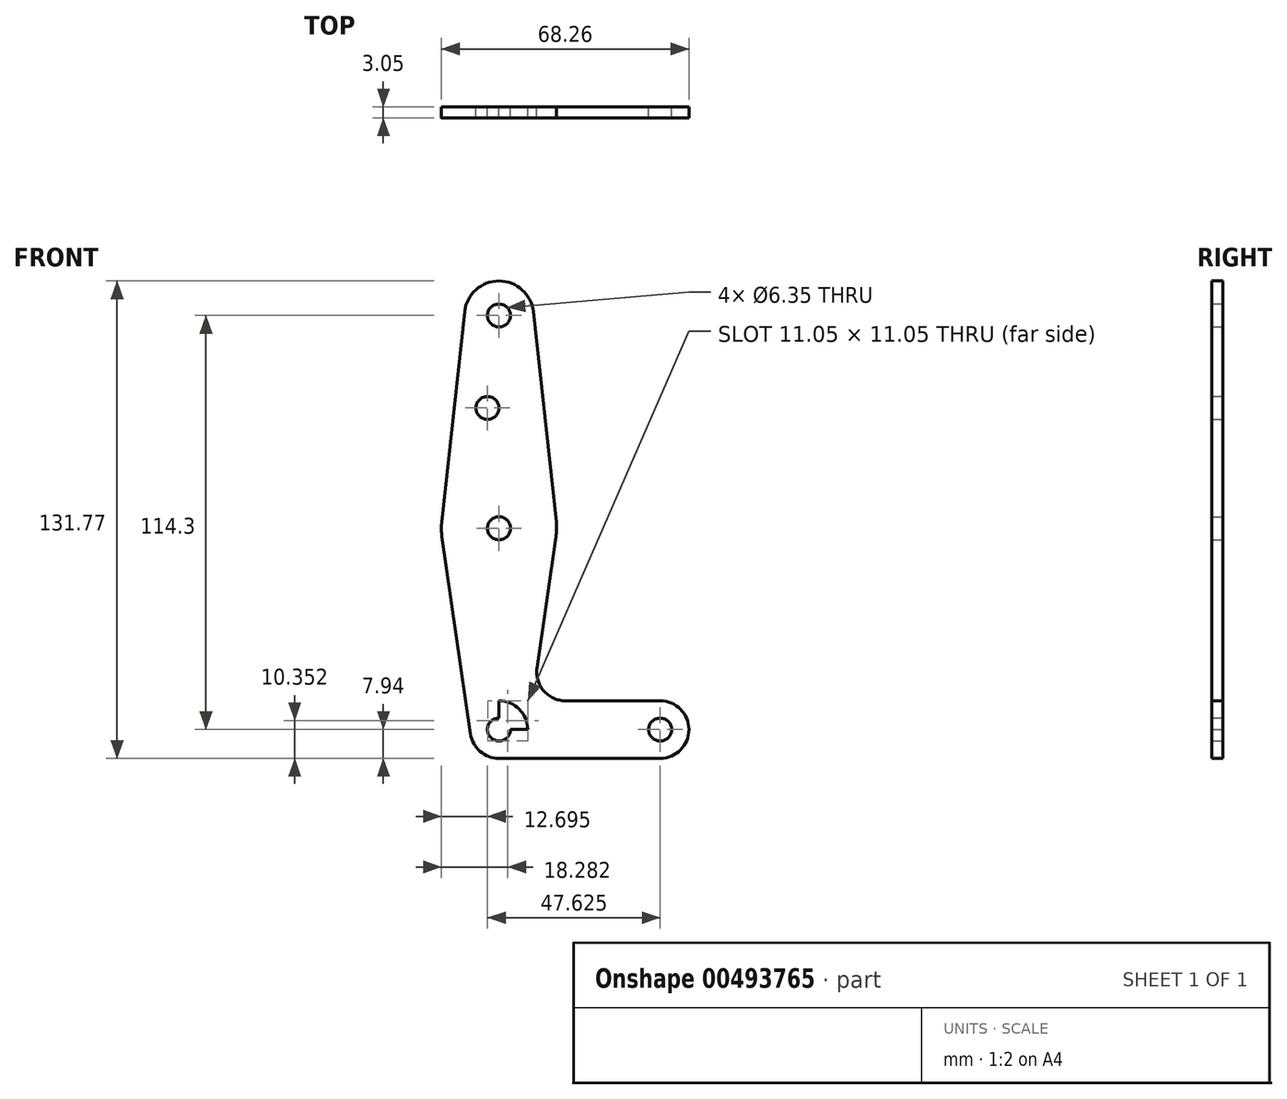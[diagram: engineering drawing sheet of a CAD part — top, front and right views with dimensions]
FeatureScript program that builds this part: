
annotation { "Feature Type Name" : "Feature", "Feature Type Description" : "" }
export const myFeature = defineFeature(function(context is Context, id is Id, definition is map)
    precondition{}
    {
        {
            var Q0;
            Q0=qCreatedBy(makeId("Front.planeOp"),FACE);
            var sketch = newSketch(context, id + "F0", { "sketchPlane" : qUnion([Q0])});
            skLineSegment(sketch, "E0", {"start": v(0, 0) * mm, "end": v(0, 114.3) * mm});
            skLineSegment(sketch, "E1", {"start": v(0, 0) * mm, "end": v(44.45, 0) * mm});
            skCircle(sketch, "E2", {"center": v(0, 0) * mm, "radius": 7.94 * mm});
            skCircle(sketch, "E3", {"center": v(0, 114.3) * mm, "radius": 9.53 * mm});
            skCircle(sketch, "E4", {"center": v(44.45, 0) * mm, "radius": 7.94 * mm});
            skCircle(sketch, "E5", {"center": v(0, 55.56) * mm, "radius": 15.87 * mm});
            skLineSegment(sketch, "E6", {"start": v(9.47, 115.33) * mm, "end": v(15.78, 57.28) * mm});
            skLineSegment(sketch, "E7", {"start": v(-9.47, 115.33) * mm, "end": v(-15.8, 57.15) * mm});
            skPoint(sketch, "E7.endSnap0", {"position": v(0, 57.15) * mm});
            skLineSegment(sketch, "E8", {"start": v(-15.71, 53.3) * mm, "end": v(-7.86, -1.13) * mm});
            skLineSegment(sketch, "E9", {"start": v(15.71, 53.3) * mm, "end": v(10.48, 17.02) * mm});
            skLineSegment(sketch, "E10", {"start": v(18.35, 7.94) * mm, "end": v(44.45, 7.94) * mm});
            skCircle(sketch, "E11", {"center": v(-3.18, 88.76) * mm, "radius": 3.18 * mm});
            skCircle(sketch, "E12", {"center": v(0, 114.3) * mm, "radius": 3.18 * mm});
            skCircle(sketch, "E13", {"center": v(0, 55.56) * mm, "radius": 3.18 * mm});
            skCircle(sketch, "E14", {"center": v(44.45, 0) * mm, "radius": 3.18 * mm});
            skLineSegment(sketch, "E15", {"start": v(0, -7.94) * mm, "end": v(44.45, -7.94) * mm});
            skCircle(sketch, "E16", {"center": v(0, 0) * mm, "radius": 3.18 * mm});
            skPoint(sketch, "E17.newPointA", {"position": v(7.86, -1.13) * mm});
            skArc(sketch, "E17.filletArc", {"start": v(10.48, 17.02) * mm, "mid": v(12.34, 10.68) * mm, "end": v(18.35, 7.94) * mm});
            skSolve(sketch);
        }
        {
            var Q0;
            Q0 = qSketchRegion(id + "F0", true);
            extrude(context, id + "F1", {"entities" : qUnion([Q0]), "depth" : 3.05 * mm});
        }
    });
